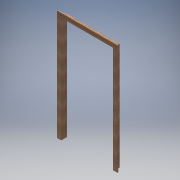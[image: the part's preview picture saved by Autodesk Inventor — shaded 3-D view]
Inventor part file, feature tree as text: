
AUTODESK INVENTOR PART (.ipt)
format: ipt  version: 2017 (Build 210142000, 142)  size: 155,648 bytes
history: native  units: mm
features: extrude x2, sketch x2, chamfer x1, mirror x1, projected_geometry x1
ambient origin geometry x8: Origin, YZ Plane, XZ Plane, XY Plane, X Axis, Y Axis, Z Axis, Center Point
bodies: Volumenkörper1 (feature_tree)
feature tree (7):
  extrude  "Extrusion1"  Depth=950.0mm
  extrude  "Extrusion2"  Depth=60.0mm
  chamfer  "Fase1"  Distance=60.0mm
  mirror  "Spiegeln1"
  sketch  "Skizze1"  dims[d0=1900.0mm d1=950.0mm]
  sketch  "Skizze2"  dims[d2=60.0mm d3=60.0mm d4=60.0mm d5=20.0mm d6=0.0mm d7=15.0mm d8=15.0mm d9=15.0mm d10=950.0mm d11=1900.0mm d12=80.0mm d13=0.0mm d14=5.0mm d15=2.0mm d16=45.0deg]
  projected_geometry  "Projizierte Kontur1"
